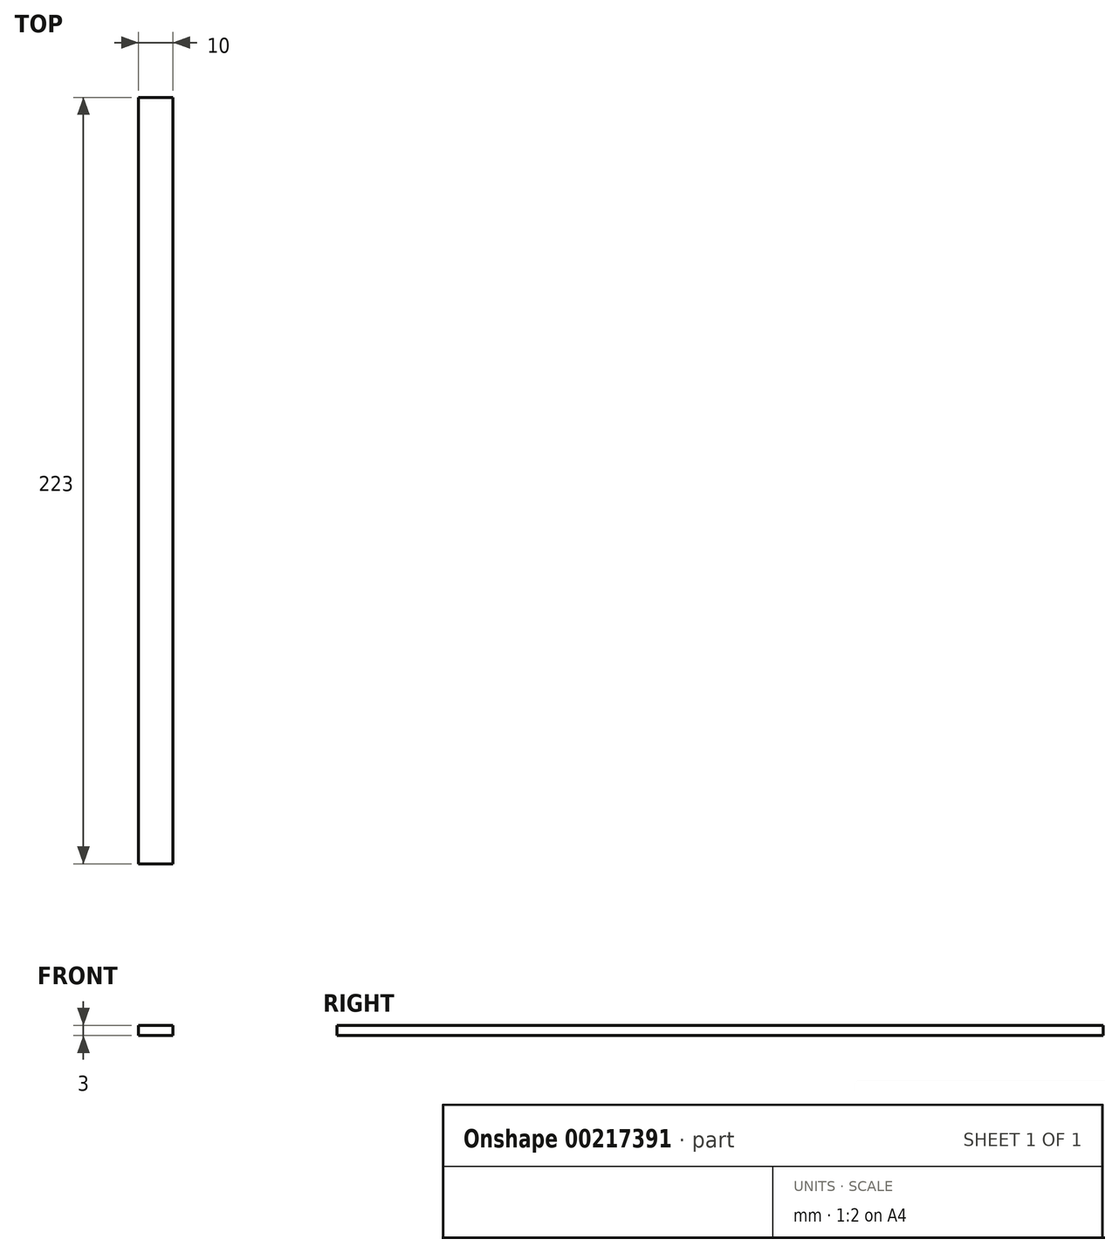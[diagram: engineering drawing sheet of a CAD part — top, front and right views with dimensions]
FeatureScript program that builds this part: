
annotation { "Feature Type Name" : "Feature", "Feature Type Description" : "" }
export const myFeature = defineFeature(function(context is Context, id is Id, definition is map)
    precondition{}
    {
        {
            var Q0;
            Q0=qCreatedBy(makeId("Top.planeOp"),FACE);
            var sketch = newSketch(context, id + "F0", { "sketchPlane" : qUnion([Q0])});
            skLineSegment(sketch, "E0.bottom", {"start": v(-130, -123) * mm, "end": v(-120, -123) * mm});
            skLineSegment(sketch, "E0.top", {"start": v(-130, 100) * mm, "end": v(-120, 100) * mm});
            skLineSegment(sketch, "E0.left", {"start": v(-130, -123) * mm, "end": v(-130, 100) * mm});
            skLineSegment(sketch, "E0.right", {"start": v(114, -123) * mm, "end": v(114, 100) * mm});
            skLineSegment(sketch, "E1.0", {"start": v(-120, -113) * mm, "end": v(-120, 90) * mm});
            skLineSegment(sketch, "E1.2", {"start": v(104, -113) * mm, "end": v(104, 90) * mm});
            skLineSegment(sketch, "E2", {"start": v(-120, -113) * mm, "end": v(-120, -123) * mm});
            skLineSegment(sketch, "E3", {"start": v(104, -113) * mm, "end": v(104, -123) * mm});
            skLineSegment(sketch, "E4.trimOffspring", {"start": v(104, -123) * mm, "end": v(114, -123) * mm});
            skLineSegment(sketch, "E5", {"start": v(104, 90) * mm, "end": v(104, 100) * mm});
            skLineSegment(sketch, "E6", {"start": v(-120, 90) * mm, "end": v(-120, 100) * mm});
            skLineSegment(sketch, "E7.trimOffspring", {"start": v(104, 100) * mm, "end": v(114, 100) * mm});
            skSolve(sketch);
        }
        {
            var Q0;
            Q0=makeQuery(id+"F0.imprint","IMPRINT",FACE,{"disambiguationData":[TD([[makeQuery(id+"F0.imprint","IMPRINT",EDGE,{"derivedFrom":sQuery(id+"F0.wireOp",EDGE,"E0.bottom")}),1.0]])]});
            extrude(context, id + "F1", {"entities" : qUnion([Q0]), "depth" : 3 * mm});
        }
    });
